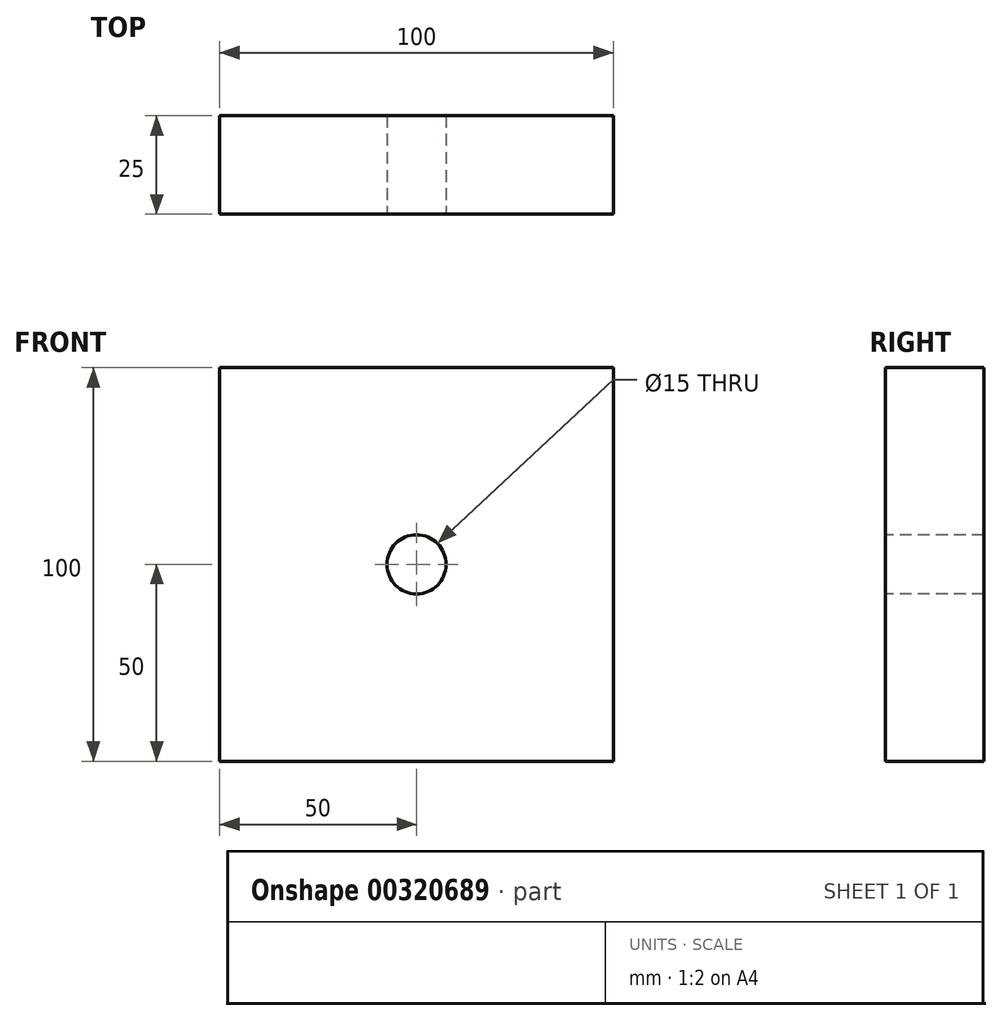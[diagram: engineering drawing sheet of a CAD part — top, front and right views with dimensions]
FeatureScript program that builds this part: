
annotation { "Feature Type Name" : "Feature", "Feature Type Description" : "" }
export const myFeature = defineFeature(function(context is Context, id is Id, definition is map)
    precondition{}
    {
        {
            var Q0;
            Q0=qCreatedBy(makeId("Front.planeOp"),FACE);
            var sketch = newSketch(context, id + "F0", { "sketchPlane" : qUnion([Q0])});
            skLineSegment(sketch, "E0.bottom", {"start": v(-50, 50) * mm, "end": v(50, 50) * mm});
            skLineSegment(sketch, "E0.top", {"start": v(-50, -50) * mm, "end": v(50, -50) * mm});
            skLineSegment(sketch, "E0.left", {"start": v(-50, 50) * mm, "end": v(-50, -50) * mm});
            skLineSegment(sketch, "E0.right", {"start": v(50, 50) * mm, "end": v(50, -50) * mm});
            skPoint(sketch, "E0.middle", {"position": v(0, 0) * mm});
            skSolve(sketch);
        }
        {
            var Q0;
            Q0 = qSketchRegion(id + "F0", true);
            extrude(context, id + "F1", {"entities" : qUnion([Q0]), "depth" : 25 * mm});
        }
        {
            var Q0;
            Q0=makeQuery(id+"F1.opExtrude","CAP_FACE",FACE,{"disambiguationData":[OSD([sQuery(id+"F0.wireOp",EDGE,"E0.bottom"),sQuery(id+"F0.wireOp",EDGE,"E0.top"),sQuery(id+"F0.wireOp",EDGE,"E0.left"),sQuery(id+"F0.wireOp",EDGE,"E0.right")])],"isStart":false});
            var sketch = newSketch(context, id + "F2", { "sketchPlane" : qUnion([Q0])});
            skCircle(sketch, "E1", {"center": v(0, 0) * mm, "radius": 7.85 * mm});
            skSolve(sketch);
        }
        {
            var Q0;
            Q0=sQuery(id+"F2.wireOp",VERTEX,"E1.center");
            var Q1;
            Q1=makeQuery(id+"F1.opExtrude","SWEPT_BODY",BODY,{"disambiguationData":[OSD([sQuery(id+"F0.wireOp",EDGE,"E0.bottom"),sQuery(id+"F0.wireOp",EDGE,"E0.top"),sQuery(id+"F0.wireOp",EDGE,"E0.left"),sQuery(id+"F0.wireOp",EDGE,"E0.right")])]});
            hole(context, id + "F3", {"style" : HoleStyle.SIMPLE, "endStyle" : HoleEndStyle.THROUGH, "holeDiameter" : 15 * mm, "tappedDepth" : 12 * mm, "tapClearance" : 3, "locations" : qUnion([Q0]), "scope" : qUnion([Q1])});
        }
    });
